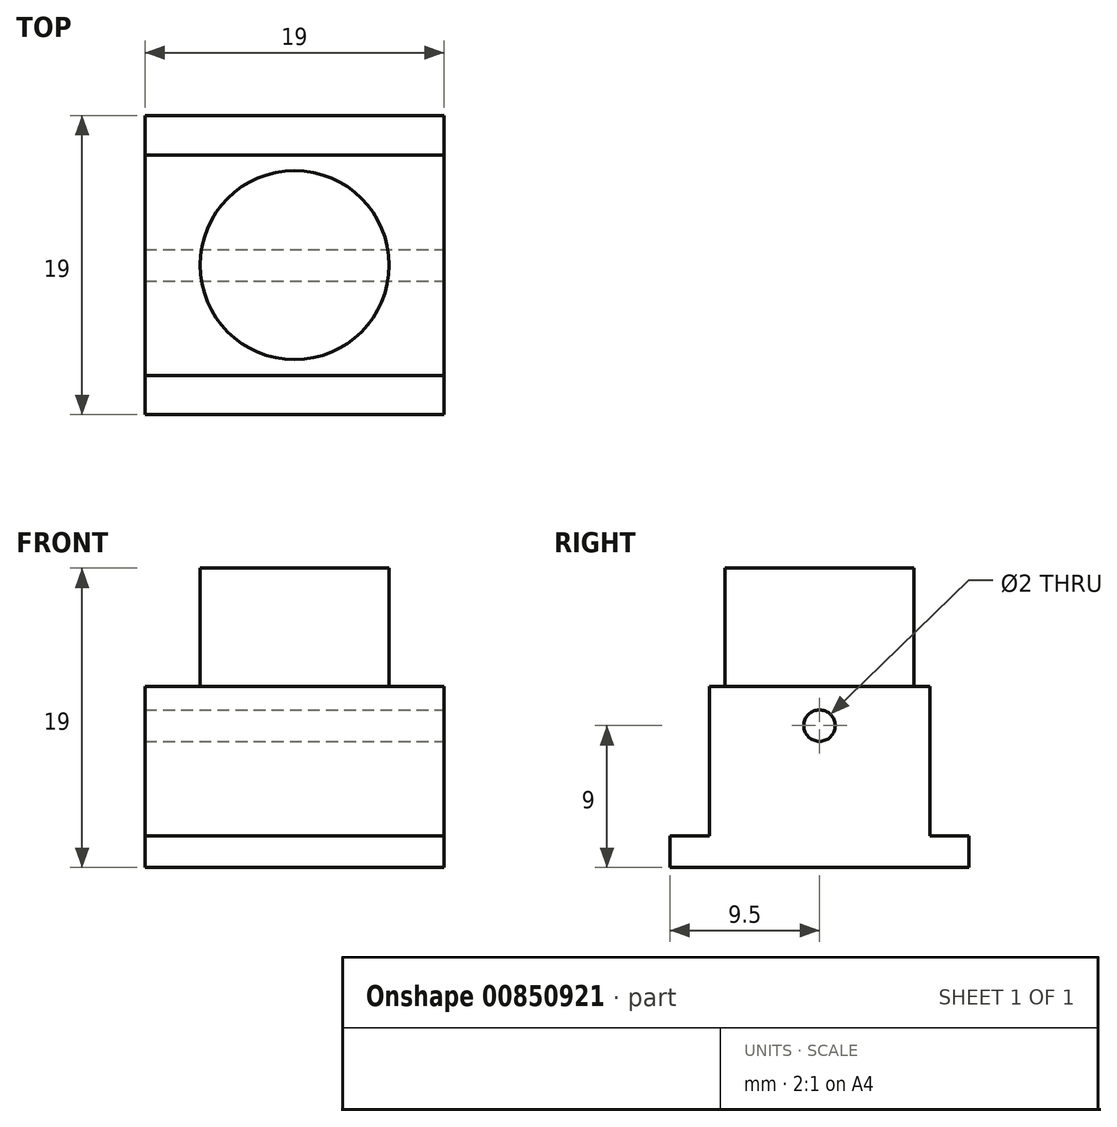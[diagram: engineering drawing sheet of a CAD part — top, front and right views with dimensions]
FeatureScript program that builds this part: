
annotation { "Feature Type Name" : "Feature", "Feature Type Description" : "" }
export const myFeature = defineFeature(function(context is Context, id is Id, definition is map)
    precondition{}
    {
        {
            var Q0;
            Q0=qCreatedBy(makeId("Top.planeOp"),FACE);
            var sketch = newSketch(context, id + "F0", { "sketchPlane" : qUnion([Q0])});
            skLineSegment(sketch, "E0.bottom", {"start": v(9.5, 9.5) * mm, "end": v(-9.5, 9.5) * mm});
            skLineSegment(sketch, "E0.top", {"start": v(9.5, -9.5) * mm, "end": v(-9.5, -9.5) * mm});
            skLineSegment(sketch, "E0.left", {"start": v(9.5, 9.5) * mm, "end": v(9.5, -9.5) * mm});
            skLineSegment(sketch, "E0.right", {"start": v(-9.5, 9.5) * mm, "end": v(-9.5, -9.5) * mm});
            skPoint(sketch, "E0.middle", {"position": v(0, 0) * mm});
            skSolve(sketch);
        }
        {
            var Q0;
            Q0=qCreatedBy(makeId("Top.planeOp"),FACE);
            var sketch = newSketch(context, id + "F1", { "sketchPlane" : qUnion([Q0])});
            skCircle(sketch, "E1", {"center": v(0, 0) * mm, "radius": 6 * mm});
            skSolve(sketch);
        }
        {
            var Q0;
            Q0=qCreatedBy(makeId("Top.planeOp"),FACE);
            var sketch = newSketch(context, id + "F2", { "sketchPlane" : qUnion([Q0])});
            skLineSegment(sketch, "E2.bottom", {"start": v(-9.5, 7) * mm, "end": v(9.5, 7) * mm});
            skLineSegment(sketch, "E2.top", {"start": v(-9.5, -7) * mm, "end": v(9.5, -7) * mm});
            skLineSegment(sketch, "E2.left", {"start": v(-9.5, 7) * mm, "end": v(-9.5, -7) * mm});
            skLineSegment(sketch, "E2.right", {"start": v(9.5, 7) * mm, "end": v(9.5, -7) * mm});
            skPoint(sketch, "E2.middle", {"position": v(0, 0) * mm});
            skSolve(sketch);
        }
        {
            var Q0;
            Q0=makeQuery(id+"F0.imprint","IMPRINT",FACE,{"disambiguationData":[TD([[makeQuery(id+"F0.imprint","IMPRINT",EDGE,{"derivedFrom":sQuery(id+"F0.wireOp",EDGE,"E0.bottom")}),1.0]])]});
            extrude(context, id + "F3", {"entities" : qUnion([Q0]), "depth" : 2 * mm, "offsetDistance" : 25 * mm});
        }
        {
            var Q0;
            Q0=qSketchRegion(id+"F2",true);
            extrude(context, id + "F4", {"entities" : qUnion([Q0]), "operationType" : NewBodyOperationType.ADD, "depth" : 11.5 * mm, "offsetDistance" : 25 * mm, "hasSecondDirection" : true, "secondDirectionOppositeDirection" : false, "secondDirectionDepth" : 2 * mm});
        }
        {
            var Q0;
            Q0=qSketchRegion(id+"F1",true);
            extrude(context, id + "F5", {"entities" : qUnion([Q0]), "operationType" : NewBodyOperationType.ADD, "depth" : 19 * mm, "offsetDistance" : 25 * mm, "hasSecondDirection" : true, "secondDirectionOppositeDirection" : false, "secondDirectionDepth" : 11.5 * mm});
        }
        {
            var Q0;
            Q0=qCreatedBy(makeId("Right.planeOp"),FACE);
            var sketch = newSketch(context, id + "F6", { "sketchPlane" : qUnion([Q0])});
            skLineSegment(sketch, "E3", {"start": v(0, 0) * mm, "end": v(0, 9) * mm, "construction": true});
            skCircle(sketch, "E4", {"center": v(0, 9) * mm, "radius": 1 * mm});
            skSolve(sketch);
        }
        {
            var Q0;
            Q0=qSketchRegion(id+"F6",true);
            extrude(context, id + "F7", {"entities" : qUnion([Q0]), "operationType" : NewBodyOperationType.REMOVE, "oppositeDirection" : true, "depth" : 25 * mm, "offsetDistance" : 25 * mm, "hasSecondDirection" : true, "secondDirectionOppositeDirection" : false, "secondDirectionDepth" : 25 * mm});
        }
    });
